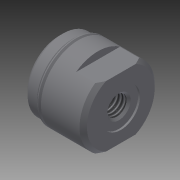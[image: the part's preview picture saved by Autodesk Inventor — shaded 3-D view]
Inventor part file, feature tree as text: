
AUTODESK INVENTOR PART (.ipt)
format: ipt  version: 2014 (Build 180170000, 170)  size: 200,192 bytes
history: native  units: in
note: dims shown in document units (in); Inventor stores cm internally (conversion verified against a paired STEP export)
features: other x63, sketch x5, revolve x3, extrude x1, hole x1, thread x1
ambient origin geometry x8: Origin, YZ Plane, XZ Plane, XY Plane, X Axis, Y Axis, Z Axis, Center Point
bodies: Solid1 (feature_tree)
feature tree (74):
  revolve  "Revolution1"  [1 undecoded]
  extrude  "Extrusion1"  TaperAngle=360.0deg  [1 undecoded]
  hole  "Hole1"  [1 undecoded]
  revolve  "Revolution2"  [1 undecoded]
  thread  "Thread1"  [1 undecoded]
  revolve  "Revolution3"  [1 undecoded]
  other  "aa2_XY"
  other  "aa2_YZ"
  other  "aa2_ZX"
  other  "aa2_X"
  other  "aa2_Y"
  other  "aa2_Z"
  other  "aa2_Center"
  other  "m1_XY"
  other  "m1_YZ"
  other  "m1_ZX"
  other  "m1_X"
  other  "m1_Y"
  other  "m1_Z"
  other  "m1_Center"
  other  "m2_XY"
  other  "m2_YZ"
  other  "m2_ZX"
  other  "m2_X"
  other  "m2_Y"
  other  "m2_Z"
  other  "m2_Center"
  other  "n1_XY"
  other  "n1_YZ"
  other  "n1_ZX"
  other  "n1_X"
  other  "n1_Y"
  other  "n1_Z"
  other  "n1_Center"
  other  "n2_XY"
  other  "n2_YZ"
  other  "n2_ZX"
  other  "n2_X"
  other  "n2_Y"
  other  "n2_Z"
  other  "n2_Center"
  other  "rear_head_XY"
  other  "rear_head_YZ"
  other  "rear_head_ZX"
  other  "rear_head_X"
  other  "rear_head_Y"
  other  "rear_head_Z"
  other  "rear_head_Center"
  other  "to_bushing_XY"
  other  "to_bushing_YZ"
  other  "to_bushing_ZX"
  other  "to_bushing_X"
  other  "to_bushing_Y"
  other  "to_bushing_Z"
  other  "to_bushing_Center"
  other  "to_mounting_bracket_xp_XY"
  other  "to_mounting_bracket_xp_YZ"
  other  "to_mounting_bracket_xp_ZX"
  other  "to_mounting_bracket_xp_X"
  other  "to_mounting_bracket_xp_Y"
  other  "to_mounting_bracket_xp_Z"
  other  "to_mounting_bracket_xp_Center"
  other  "to_pivot_bracket_XY"
  other  "to_pivot_bracket_YZ"
  other  "to_pivot_bracket_ZX"
  other  "to_pivot_bracket_X"
  other  "to_pivot_bracket_Y"
  other  "to_pivot_bracket_Z"
  other  "to_pivot_bracket_Center"
  sketch  "Sketch_1"  dims[d0=360.0deg d1=0.185in d2=0.0in]
  sketch  "Sketch_2"  dims[d3=0.375in d4=0.75in d5=0.395in d6=0.25in d7=90.0deg d8=0.188in d9=0.0in d10=360.0deg]
  sketch  "Sketch3"  dims[d11=0.185in d12=0.112in d13=360.0deg]
  sketch  "Sketch_5"
  sketch  "Sketch_9"
note: 6 required parameter values undecoded (feature->parameter linkage not recoverable at this tier; creation-order binding heuristic only, values carry confidence <= 0.55)